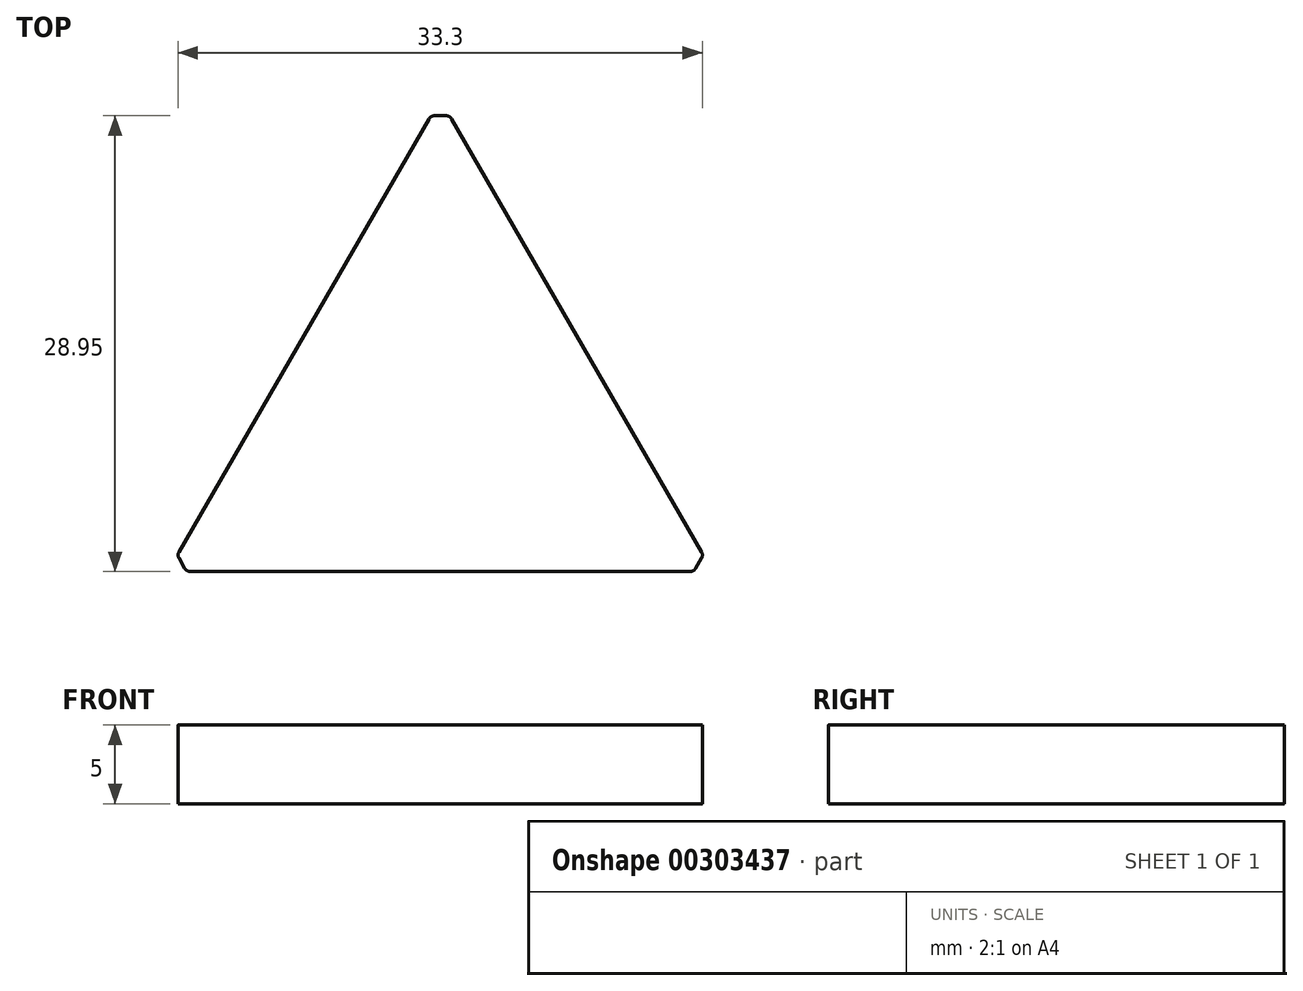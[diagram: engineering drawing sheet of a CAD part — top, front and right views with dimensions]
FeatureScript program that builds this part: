
annotation { "Feature Type Name" : "Feature", "Feature Type Description" : "" }
export const myFeature = defineFeature(function(context is Context, id is Id, definition is map)
    precondition{}
    {
        {
            var Q0;
            Q0=qCreatedBy(makeId("Top.planeOp"),FACE);
            var sketch = newSketch(context, id + "F0", { "sketchPlane" : qUnion([Q0])});
            skLineSegment(sketch, "E0", {"start": v(-17.32, -15) * mm, "end": v(17.32, -15) * mm});
            skLineSegment(sketch, "E1", {"start": v(17.32, -15) * mm, "end": v(0, 15) * mm});
            skLineSegment(sketch, "E2", {"start": v(0, 15) * mm, "end": v(-17.32, -15) * mm});
            skSolve(sketch);
        }
        {
            var Q0;
            Q0 = qSketchRegion(id + "F0", true);
            extrude(context, id + "F1", {"entities" : qUnion([Q0]), "depth" : 5 * mm});
        }
        {
            var Q0;
            Q0=makeQuery(id+"F1.opExtrude","SWEPT_EDGE",EDGE,{"disambiguationData":[OSD([sQuery(id+"F0.wireOp",EDGE,"E0"),sQuery(id+"F0.wireOp",EDGE,"E2")])]});
            var Q1;
            Q1=makeQuery(id+"F1.opExtrude","SWEPT_EDGE",EDGE,{"disambiguationData":[OSD([sQuery(id+"F0.wireOp",EDGE,"E0"),sQuery(id+"F0.wireOp",EDGE,"E1")])]});
            var Q2;
            Q2=makeQuery(id+"F1.opExtrude","SWEPT_EDGE",EDGE,{"disambiguationData":[OSD([sQuery(id+"F0.wireOp",EDGE,"E1"),sQuery(id+"F0.wireOp",EDGE,"E2")])]});
            chamfer(context, id + "F2", {"entities" : qUnion([Q0, Q1, Q2]), "width" : 0.7 * mm, "tangentPropagation" : true});
        }
        {
            var Q0;
            {var subQ0=sQuery(id+"F0.wireOp",EDGE,"E2");Q0=makeQuery(id+"F2.opChamfer","BLEND_EDGE",EDGE,{"blendedFrom":[makeQuery(id+"F1.opExtrude","SWEPT_EDGE",EDGE,{"disambiguationData":[OSD([sQuery(id+"F0.wireOp",EDGE,"E1"),subQ0])]}),makeQuery(id+"F1.opExtrude","SWEPT_FACE",FACE,{"disambiguationData":[OSD([subQ0])]})],"blendedInto":[makeQuery(id+"F1.opExtrude","SWEPT_FACE",FACE,{"disambiguationData":[OSD([subQ0])]})]});}
            var Q1;
            {var subQ0=sQuery(id+"F0.wireOp",EDGE,"E1");Q1=makeQuery(id+"F2.opChamfer","BLEND_EDGE",EDGE,{"blendedFrom":[makeQuery(id+"F1.opExtrude","SWEPT_EDGE",EDGE,{"disambiguationData":[OSD([subQ0,sQuery(id+"F0.wireOp",EDGE,"E2")])]}),makeQuery(id+"F1.opExtrude","SWEPT_FACE",FACE,{"disambiguationData":[OSD([subQ0])]})],"blendedInto":[makeQuery(id+"F1.opExtrude","SWEPT_FACE",FACE,{"disambiguationData":[OSD([subQ0])]})]});}
            var Q2;
            {var subQ0=sQuery(id+"F0.wireOp",EDGE,"E1");Q2=makeQuery(id+"F2.opChamfer","BLEND_EDGE",EDGE,{"blendedFrom":[makeQuery(id+"F1.opExtrude","SWEPT_EDGE",EDGE,{"disambiguationData":[OSD([sQuery(id+"F0.wireOp",EDGE,"E0"),subQ0])]}),makeQuery(id+"F1.opExtrude","SWEPT_FACE",FACE,{"disambiguationData":[OSD([subQ0])]})],"blendedInto":[makeQuery(id+"F1.opExtrude","SWEPT_FACE",FACE,{"disambiguationData":[OSD([subQ0])]})]});}
            var Q3;
            {var subQ0=sQuery(id+"F0.wireOp",EDGE,"E0");Q3=makeQuery(id+"F2.opChamfer","BLEND_EDGE",EDGE,{"blendedFrom":[makeQuery(id+"F1.opExtrude","SWEPT_EDGE",EDGE,{"disambiguationData":[OSD([subQ0,sQuery(id+"F0.wireOp",EDGE,"E1")])]}),makeQuery(id+"F1.opExtrude","SWEPT_FACE",FACE,{"disambiguationData":[OSD([subQ0])]})],"blendedInto":[makeQuery(id+"F1.opExtrude","SWEPT_FACE",FACE,{"disambiguationData":[OSD([subQ0])]})]});}
            var Q4;
            {var subQ0=sQuery(id+"F0.wireOp",EDGE,"E0");Q4=makeQuery(id+"F2.opChamfer","BLEND_EDGE",EDGE,{"blendedFrom":[makeQuery(id+"F1.opExtrude","SWEPT_EDGE",EDGE,{"disambiguationData":[OSD([subQ0,sQuery(id+"F0.wireOp",EDGE,"E2")])]}),makeQuery(id+"F1.opExtrude","SWEPT_FACE",FACE,{"disambiguationData":[OSD([subQ0])]})],"blendedInto":[makeQuery(id+"F1.opExtrude","SWEPT_FACE",FACE,{"disambiguationData":[OSD([subQ0])]})]});}
            var Q5;
            {var subQ0=sQuery(id+"F0.wireOp",EDGE,"E2");Q5=makeQuery(id+"F2.opChamfer","BLEND_EDGE",EDGE,{"blendedFrom":[makeQuery(id+"F1.opExtrude","SWEPT_EDGE",EDGE,{"disambiguationData":[OSD([sQuery(id+"F0.wireOp",EDGE,"E0"),subQ0])]}),makeQuery(id+"F1.opExtrude","SWEPT_FACE",FACE,{"disambiguationData":[OSD([subQ0])]})],"blendedInto":[makeQuery(id+"F1.opExtrude","SWEPT_FACE",FACE,{"disambiguationData":[OSD([subQ0])]})]});}
            fillet(context, id + "F3", {"entities" : qUnion([Q0, Q1, Q2, Q3, Q4, Q5]), "radius" : 0.4 * mm, "tangentPropagation" : true, "allowEdgeOverflow" : false});
        }
    });
